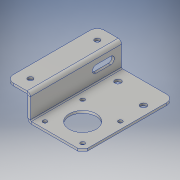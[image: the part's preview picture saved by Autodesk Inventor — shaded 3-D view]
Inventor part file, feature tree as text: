
AUTODESK INVENTOR PART (.ipt)
format: ipt  version: 2019 (Build 230136000, 136)  size: 278,016 bytes
history: native  units: mm
features: other x7, sketch x5, sheet_metal_op x3, chamfer x1
ambient origin geometry x8: Origin, YZ Plane, XZ Plane, XY Plane, X Axis, Y Axis, Z Axis, Center Point
bodies: Solid1 (feature_tree)
feature tree (16):
  sheet_metal_op  "Contour Flange1"
  other  "Corner Chamfer1"
  chamfer  "Corner Round2"
  sketch  "Sketch1"  dims[d0=20.0mm]
  other  "Plate1"
  sheet_metal_op  "Bend1"
  sheet_metal_op  "Corner1"
  sketch  "Sketch2"  dims[d1=20.0mm]
  sketch  "Sketch3"  dims[d2=43.0mm]
  sketch  "Sketch4"  dims[d3=2.0mm]
  sketch  "Sketch16"  dims[d4=0.5mm d5=0.5mm d6=0.5mm d7=0.8mm d8=75.0mm d9=0.8mm d10=2.0mm d11=0.5mm d12=2.0mm d13=0.5mm d14=22.2mm d15=31.0mm d16=3.4mm d17=2.0mm d18=0.0mm d19=4.0mm d20=6.0mm d21=45.0deg d22=4.2mm d25=2.0mm d26=0.0mm d28=10.0mm d30=10.0mm d32=5.0mm d33=7.5mm d36=35.0mm d37=2.0mm d38=0.0mm d41=5.565mm d42=17.5mm d43=11.0mm d143=6.0mm d149=12.0mm d150=6.0mm d151=15.0mm d152=2.0mm d153=0.0mm]
  other  "Cut1"
  other  "Cut2"
  other  "Cut3"
  other  "Cut5"
  other  "Definition1"
